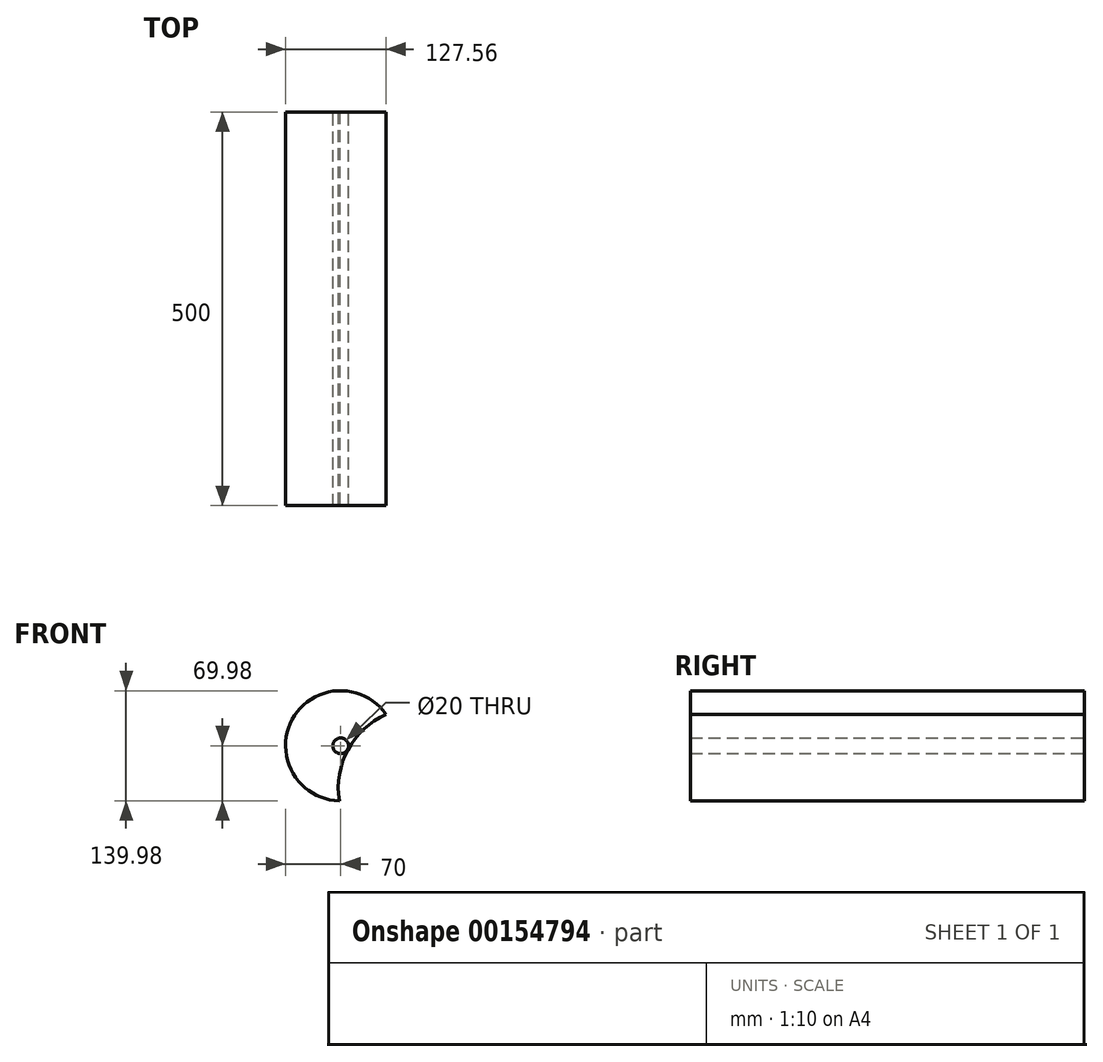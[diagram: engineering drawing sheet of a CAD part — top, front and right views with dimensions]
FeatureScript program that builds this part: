
annotation { "Feature Type Name" : "Feature", "Feature Type Description" : "" }
export const myFeature = defineFeature(function(context is Context, id is Id, definition is map)
    precondition{}
    {
        {
            var Q0;
            Q0=qCreatedBy(makeId("Front.planeOp"),FACE);
            var sketch = newSketch(context, id + "F0", { "sketchPlane" : qUnion([Q0])});
            skCircle(sketch, "E0", {"center": v(0, 0) * mm, "radius": 10 * mm});
            skCircle(sketch, "E1", {"center": v(0, 0) * mm, "radius": 70 * mm});
            skSolve(sketch);
        }
        {
            var Q0;
            Q0 = qSketchRegion(id + "F0", true);
            extrude(context, id + "F1", {"entities" : qUnion([Q0]), "depth" : 500 * mm});
        }
        {
            var Q0;
            Q0=makeQuery(id+"F1.opExtrude","CAP_FACE",FACE,{"disambiguationData":[OSD([sQuery(id+"F0.wireOp",EDGE,"E0"),sQuery(id+"F0.wireOp",EDGE,"E1")])],"isStart":false});
            var sketch = newSketch(context, id + "F2", { "sketchPlane" : qUnion([Q0])});
            skCircle(sketch, "E2", {"center": v(99.4, -53.74) * mm, "radius": 102.5 * mm});
            skSolve(sketch);
        }
        {
            var Q0;
            Q0 = qSketchRegion(id + "F2", true);
            extrude(context, id + "F3", {"entities" : qUnion([Q0]), "operationType" : NewBodyOperationType.REMOVE, "oppositeDirection" : true, "depth" : 600 * mm});
        }
    });
